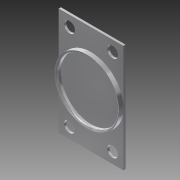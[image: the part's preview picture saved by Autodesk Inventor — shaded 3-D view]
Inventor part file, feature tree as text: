
AUTODESK INVENTOR PART (.ipt)
format: ipt  version: 2014 (Build 180170000, 170)  size: 123,392 bytes
history: native  units: mm
features: extrude x2, fillet x2, sketch x1
ambient origin geometry x8: Origin, YZ Plane, XZ Plane, XY Plane, X Axis, Y Axis, Z Axis, Center Point
bodies: Solid1 (feature_tree)
feature tree (5):
  sketch  "Sketch1"  dims[d0=30.0mm d1=50.0mm d2=5.0mm d3=5.0mm d4=5.0mm d5=5.0mm d6=5.0mm d7=30.0mm d8=28.0mm d9=1.0mm d10=0.0mm d11=3.0mm d12=0.0mm d13=1.0mm d14=1.0mm]
  extrude  "Extrusion1"  Depth=50.0mm
  extrude  "Extrusion2"  Depth=1.0mm
  fillet  "Fillet1"  Radius=5.0mm
  fillet  "Fillet2"  Radius=5.0mm
